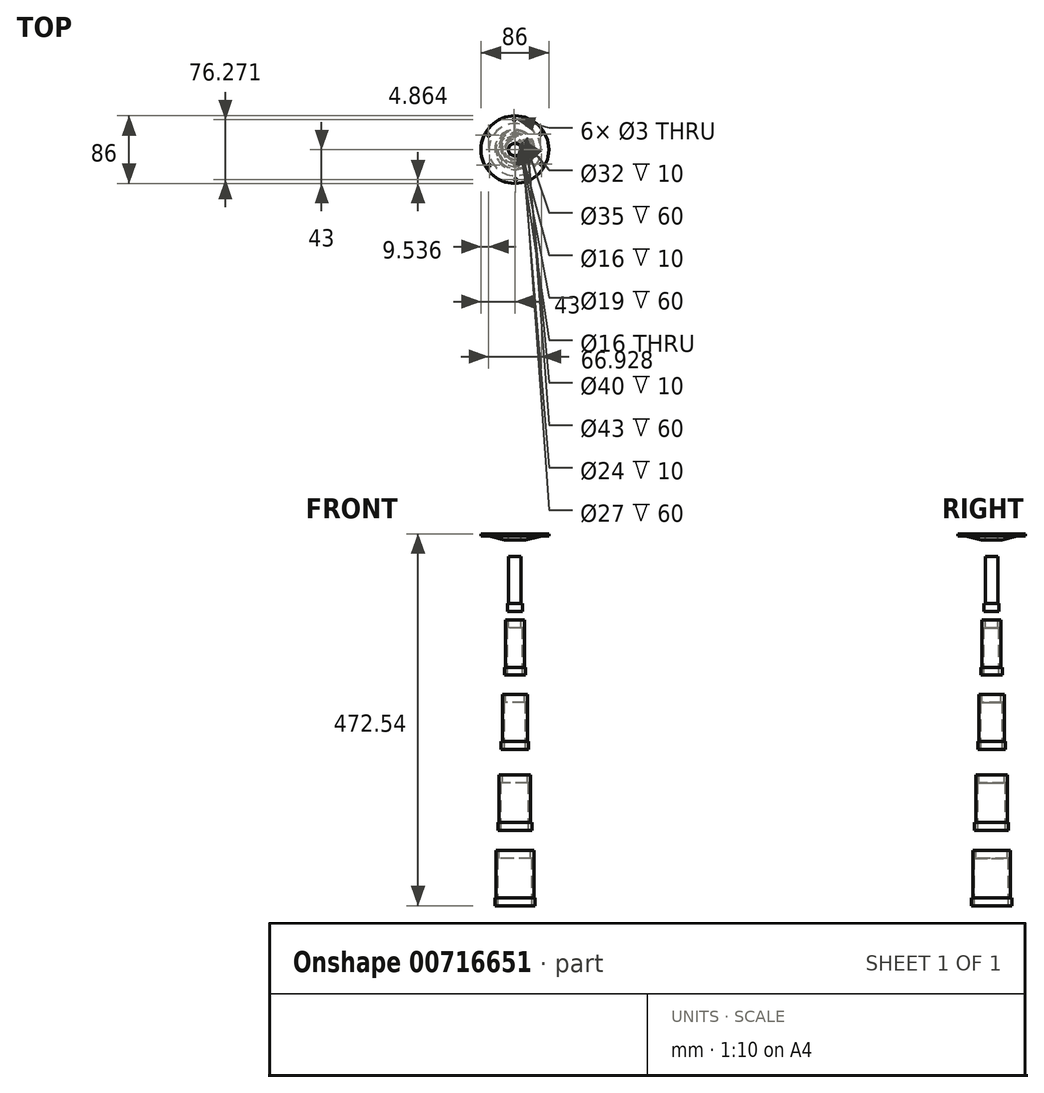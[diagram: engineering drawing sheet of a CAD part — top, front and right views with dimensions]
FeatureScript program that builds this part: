
annotation { "Feature Type Name" : "Feature", "Feature Type Description" : "" }
export const myFeature = defineFeature(function(context is Context, id is Id, definition is map)
    precondition{}
    {
        {
            var Q0;
            Q0=qCreatedBy(makeId("Front.planeOp"),FACE);
            var sketch = newSketch(context, id + "F0", { "sketchPlane" : qUnion([Q0])});
            skLineSegment(sketch, "E0", {"start": v(0, 139.43) * mm, "end": v(0, -479.87) * mm});
            skLineSegment(sketch, "E1", {"start": v(0, 29.1) * mm, "end": v(-8, 29.1) * mm});
            skLineSegment(sketch, "E2", {"start": v(-8, 29.1) * mm, "end": v(-8, -30.9) * mm});
            skLineSegment(sketch, "E3", {"start": v(-8, -30.9) * mm, "end": v(-9.5, -30.9) * mm});
            skLineSegment(sketch, "E4", {"start": v(-9.5, -30.9) * mm, "end": v(-9.5, -40.9) * mm});
            skLineSegment(sketch, "E5", {"start": v(-9.5, -40.9) * mm, "end": v(0, -40.9) * mm});
            skLineSegment(sketch, "E6", {"start": v(-8, -51.8) * mm, "end": v(-8, -61.8) * mm});
            skLineSegment(sketch, "E7", {"start": v(-8, -61.8) * mm, "end": v(-9.5, -61.8) * mm});
            skLineSegment(sketch, "E8", {"start": v(-9.5, -61.8) * mm, "end": v(-9.5, -121.8) * mm});
            skLineSegment(sketch, "E9", {"start": v(-8, -51.8) * mm, "end": v(-12, -51.8) * mm});
            skLineSegment(sketch, "E10", {"start": v(-12, -51.8) * mm, "end": v(-12, -111.8) * mm});
            skLineSegment(sketch, "E11", {"start": v(-12, -111.8) * mm, "end": v(-13.5, -111.8) * mm});
            skLineSegment(sketch, "E12", {"start": v(-13.5, -111.8) * mm, "end": v(-13.5, -121.8) * mm});
            skLineSegment(sketch, "E13", {"start": v(-13.5, -121.8) * mm, "end": v(-9.5, -121.8) * mm});
            skLineSegment(sketch, "E14", {"start": v(-8, 29.1) * mm, "end": v(-8, 19.1) * mm});
            skLineSegment(sketch, "E15", {"start": v(-12, -146.28) * mm, "end": v(-12, -156.28) * mm});
            skLineSegment(sketch, "E16", {"start": v(-12, -156.28) * mm, "end": v(-13.5, -156.28) * mm});
            skLineSegment(sketch, "E17", {"start": v(-13.5, -156.28) * mm, "end": v(-13.5, -216.28) * mm});
            skLineSegment(sketch, "E18", {"start": v(-12, -146.28) * mm, "end": v(-16, -146.28) * mm});
            skLineSegment(sketch, "E19", {"start": v(-16, -146.28) * mm, "end": v(-16, -206.28) * mm});
            skLineSegment(sketch, "E20", {"start": v(-16, -206.28) * mm, "end": v(-17.5, -206.28) * mm});
            skLineSegment(sketch, "E21", {"start": v(-17.5, -206.28) * mm, "end": v(-17.5, -216.28) * mm});
            skLineSegment(sketch, "E22", {"start": v(-17.5, -216.28) * mm, "end": v(-13.5, -216.28) * mm});
            skLineSegment(sketch, "E23", {"start": v(-16, -248.87) * mm, "end": v(-16, -258.87) * mm});
            skLineSegment(sketch, "E24", {"start": v(-16, -258.87) * mm, "end": v(-17.5, -258.87) * mm});
            skLineSegment(sketch, "E25", {"start": v(-17.5, -258.87) * mm, "end": v(-17.5, -318.87) * mm});
            skLineSegment(sketch, "E26", {"start": v(-16, -248.87) * mm, "end": v(-20, -248.87) * mm});
            skLineSegment(sketch, "E27", {"start": v(-20, -248.87) * mm, "end": v(-20, -308.87) * mm});
            skLineSegment(sketch, "E28", {"start": v(-20, -308.87) * mm, "end": v(-21.5, -308.87) * mm});
            skLineSegment(sketch, "E29", {"start": v(-21.5, -308.87) * mm, "end": v(-21.5, -318.87) * mm});
            skLineSegment(sketch, "E30", {"start": v(-21.5, -318.87) * mm, "end": v(-17.5, -318.87) * mm});
            skLineSegment(sketch, "E31", {"start": v(-20, -344.77) * mm, "end": v(-20, -354.77) * mm});
            skLineSegment(sketch, "E32", {"start": v(-20, -354.77) * mm, "end": v(-21.5, -354.77) * mm});
            skLineSegment(sketch, "E33", {"start": v(-21.5, -354.77) * mm, "end": v(-21.5, -414.77) * mm});
            skLineSegment(sketch, "E34", {"start": v(-20, -344.77) * mm, "end": v(-24, -344.77) * mm});
            skLineSegment(sketch, "E35", {"start": v(-24, -344.77) * mm, "end": v(-24, -404.77) * mm});
            skLineSegment(sketch, "E36", {"start": v(-24, -404.77) * mm, "end": v(-25.5, -404.77) * mm});
            skLineSegment(sketch, "E37", {"start": v(-25.5, -404.77) * mm, "end": v(-25.5, -414.77) * mm});
            skLineSegment(sketch, "E38", {"start": v(-25.5, -414.77) * mm, "end": v(-21.5, -414.77) * mm});
            skLineSegment(sketch, "E39", {"start": v(-8, 49.77) * mm, "end": v(-8, 57.77) * mm});
            skLineSegment(sketch, "E40", {"start": v(-8, 57.77) * mm, "end": v(-43, 57.77) * mm});
            skLineSegment(sketch, "E41", {"start": v(-43, 57.77) * mm, "end": v(-43, 54.77) * mm});
            skLineSegment(sketch, "E42", {"start": v(-8, 49.77) * mm, "end": v(-13, 49.77) * mm});
            skLineSegment(sketch, "E43", {"start": v(-43, 54.77) * mm, "end": v(-33, 54.77) * mm});
            skLineSegment(sketch, "E44", {"start": v(-33, 54.77) * mm, "end": v(-13, 49.77) * mm});
            skSolve(sketch);
        }
        {
            var Q0;
            {var subQ1=sQuery(id+"F0.wireOp",EDGE,"E1");Q0=makeQuery(id+"F0.imprint","IMPRINT",FACE,{"disambiguationData":[TD([[makeQuery(id+"F0.imprint","IMPRINT",EDGE,{"derivedFrom":subQ1}),1.0]])]});}
            var Q1;
            Q1=makeQuery(id+"F0.imprint","IMPRINT",FACE,{"disambiguationData":[TD([[makeQuery(id+"F0.imprint","IMPRINT",EDGE,{"derivedFrom":sQuery(id+"F0.wireOp",EDGE,"E6")}),-1.0]])]});
            var Q2;
            Q2=makeQuery(id+"F0.imprint","IMPRINT",FACE,{"disambiguationData":[TD([[makeQuery(id+"F0.imprint","IMPRINT",EDGE,{"derivedFrom":sQuery(id+"F0.wireOp",EDGE,"E15")}),-1.0]])]});
            var Q3;
            Q3=makeQuery(id+"F0.imprint","IMPRINT",FACE,{"disambiguationData":[TD([[makeQuery(id+"F0.imprint","IMPRINT",EDGE,{"derivedFrom":sQuery(id+"F0.wireOp",EDGE,"E23")}),-1.0]])]});
            var Q4;
            Q4=makeQuery(id+"F0.imprint","IMPRINT",FACE,{"disambiguationData":[TD([[makeQuery(id+"F0.imprint","IMPRINT",EDGE,{"derivedFrom":sQuery(id+"F0.wireOp",EDGE,"E31")}),-1.0]])]});
            var Q5;
            Q5=makeQuery(id+"F0.imprint","IMPRINT",FACE,{"disambiguationData":[TD([[makeQuery(id+"F0.imprint","IMPRINT",EDGE,{"derivedFrom":sQuery(id+"F0.wireOp",EDGE,"E39")}),1.0]])]});
            var Q6;
            Q6=sQuery(id+"F0.wireOp",EDGE,"E0");
            revolve(context, id + "F1", {"entities" : qUnion([Q0, Q1, Q2, Q3, Q4, Q5]), "axis" : qUnion([Q6]), "revolveType" : RevolveType.FULL, "surfaceOperationType" : NewSurfaceOperationType.NEW});
        }
        {
            var Q0;
            Q0=makeQuery(id+"F1.opRevolve","SWEPT_FACE",FACE,{"disambiguationData":[OSD([sQuery(id+"F0.wireOp",EDGE,"E40")])]});
            var sketch = newSketch(context, id + "F2", { "sketchPlane" : qUnion([Q0])});
            skCircle(sketch, "E45", {"center": v(0.88, -38.14) * mm, "radius": 1.5 * mm});
            skCircle(sketch, "E46.1.0", {"center": v(33.46, -18.3) * mm, "radius": 1.5 * mm});
            skCircle(sketch, "E46.2.0", {"center": v(32.59, 19.83) * mm, "radius": 1.5 * mm});
            skCircle(sketch, "E46.3.0", {"center": v(-0.88, 38.14) * mm, "radius": 1.5 * mm});
            skCircle(sketch, "E46.4.0", {"center": v(-33.46, 18.3) * mm, "radius": 1.5 * mm});
            skCircle(sketch, "E46.5.0", {"center": v(-32.59, -19.83) * mm, "radius": 1.5 * mm});
            skPoint(sketch, "E46.center", {"position": v(0, 0) * mm});
            skSolve(sketch);
        }
        {
            var Q0;
            Q0=makeQuery(id+"F2.imprint","IMPRINT",FACE,{"disambiguationData":[TD([[makeQuery(id+"F2.imprint","IMPRINT",EDGE,{"derivedFrom":sQuery(id+"F2.wireOp",EDGE,"E46.4.0")}),1.0]])]});
            var Q1;
            Q1=makeQuery(id+"F2.imprint","IMPRINT",FACE,{"disambiguationData":[TD([[makeQuery(id+"F2.imprint","IMPRINT",EDGE,{"derivedFrom":sQuery(id+"F2.wireOp",EDGE,"E46.5.0")}),1.0]])]});
            var Q2;
            Q2=makeQuery(id+"F2.imprint","IMPRINT",FACE,{"disambiguationData":[TD([[makeQuery(id+"F2.imprint","IMPRINT",EDGE,{"derivedFrom":sQuery(id+"F2.wireOp",EDGE,"E45")}),1.0]])]});
            var Q3;
            Q3=makeQuery(id+"F2.imprint","IMPRINT",FACE,{"disambiguationData":[TD([[makeQuery(id+"F2.imprint","IMPRINT",EDGE,{"derivedFrom":sQuery(id+"F2.wireOp",EDGE,"E46.1.0")}),1.0]])]});
            var Q4;
            Q4=makeQuery(id+"F2.imprint","IMPRINT",FACE,{"disambiguationData":[TD([[makeQuery(id+"F2.imprint","IMPRINT",EDGE,{"derivedFrom":sQuery(id+"F2.wireOp",EDGE,"E46.2.0")}),1.0]])]});
            var Q5;
            Q5=makeQuery(id+"F2.imprint","IMPRINT",FACE,{"disambiguationData":[TD([[makeQuery(id+"F2.imprint","IMPRINT",EDGE,{"derivedFrom":sQuery(id+"F2.wireOp",EDGE,"E46.3.0")}),1.0]])]});
            extrude(context, id + "F3", {"entities" : qUnion([Q0, Q1, Q2, Q3, Q4, Q5]), "operationType" : NewBodyOperationType.REMOVE, "oppositeDirection" : true, "depth" : 25 * mm, "offsetDistance" : 25 * mm});
        }
    });
